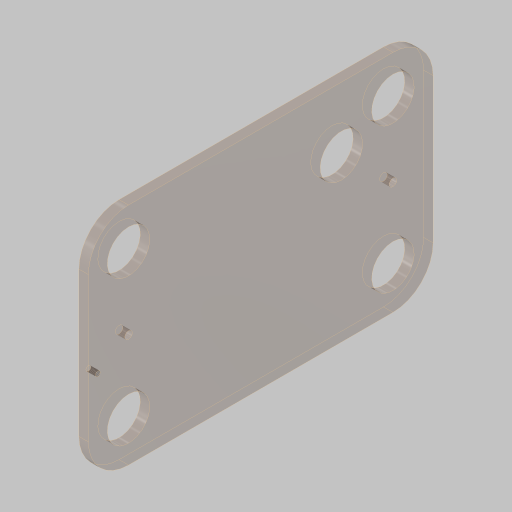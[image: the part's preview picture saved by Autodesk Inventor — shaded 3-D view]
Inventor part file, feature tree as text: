
AUTODESK INVENTOR PART (.ipt)
format: ipt  version: 2023.5 (Build 275446000, 446)  size: 160,256 bytes
history: native  units: in
note: dims shown in document units (in); Inventor stores cm internally (conversion verified against a paired STEP export)
features: sketch x2, extrude x2, hole x2
ambient origin geometry x8: Origin, YZ Plane, XZ Plane, XY Plane, X Axis, Y Axis, Z Axis, Center Point
bodies: Solid1 (feature_tree)
feature tree (6):
  sketch  "Sketch1"  dims[d0=1.125in d2=12.0in]
  extrude  "Extrusion1"  Depth=12.0in
  hole  "Hole1"  [1 undecoded]
  hole  "Hole2"  [1 undecoded]
  extrude  "Extrusion2"  Depth=7.0in
  sketch  "Sketch3"  dims[d3=4.5in d4=3.0in d6=0.25in d7=0.5in d8=3.8356in d9=0.25in d10=0.0in d11=0.201in d12=0.38in d13=0.385in d14=0.25in d15=0.5635in d16=1.0in d17=0.8108in d18=0.25in d29=0.25in d30=2.5in d31=0.13in d32=0.328in d33=0.375in d34=0.25in d35=0.5635in d36=0.25in d37=0.8108in d38=7.0in d40=1.5in d41=5.6693in d42=0.0in d43=0.0in]
note: 2 required parameter values undecoded (feature->parameter linkage not recoverable at this tier; creation-order binding heuristic only, values carry confidence <= 0.55)
